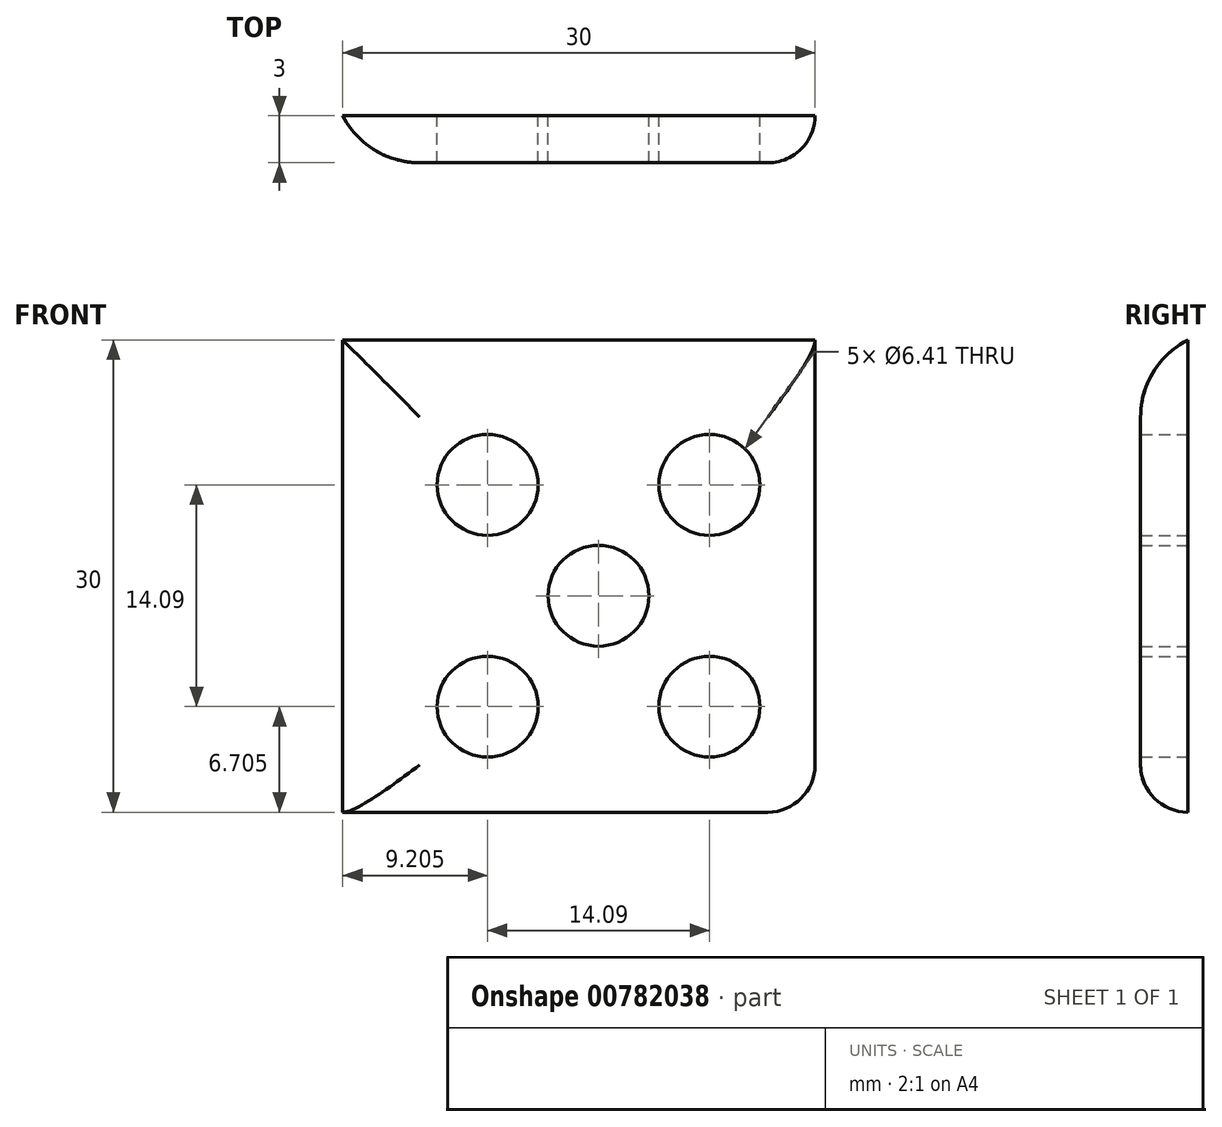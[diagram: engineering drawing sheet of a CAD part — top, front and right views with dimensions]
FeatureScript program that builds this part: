
annotation { "Feature Type Name" : "Feature", "Feature Type Description" : "" }
export const myFeature = defineFeature(function(context is Context, id is Id, definition is map)
    precondition{}
    {
        {
            var Q0;
            Q0=qCreatedBy(makeId("Front.planeOp"),FACE);
            var sketch = newSketch(context, id + "F0", { "sketchPlane" : qUnion([Q0])});
            skLineSegment(sketch, "E0.bottom", {"start": v(0, 0) * mm, "end": v(27, 0) * mm});
            skLineSegment(sketch, "E0.top", {"start": v(0, 30) * mm, "end": v(30, 30) * mm});
            skLineSegment(sketch, "E0.left", {"start": v(0, 0) * mm, "end": v(0, 30) * mm});
            skLineSegment(sketch, "E0.right", {"start": v(30, 3) * mm, "end": v(30, 30) * mm});
            skPoint(sketch, "E1", {"position": v(5.5, 30) * mm});
            skPoint(sketch, "E2", {"position": v(0, 24.5) * mm});
            skPoint(sketch, "E3", {"position": v(0, 3) * mm});
            skPoint(sketch, "E4", {"position": v(5.5, 0) * mm});
            skPoint(sketch, "E5", {"position": v(27, 0) * mm});
            skPoint(sketch, "E6", {"position": v(30, 3) * mm});
            skPoint(sketch, "E7", {"position": v(30, 24.5) * mm});
            skPoint(sketch, "E8", {"position": v(27, 30) * mm});
            skLineSegment(sketch, "E9", {"start": v(5.5, 0) * mm, "end": v(5.5, 30) * mm});
            skLineSegment(sketch, "E10", {"start": v(0, 24.5) * mm, "end": v(30, 24.5) * mm});
            skLineSegment(sketch, "E11", {"start": v(27, 30) * mm, "end": v(27, 0) * mm});
            skLineSegment(sketch, "E12", {"start": v(30, 3) * mm, "end": v(0, 3) * mm});
            skCircle(sketch, "E13", {"center": v(9.2, 6.7) * mm, "radius": 3.2 * mm});
            skCircle(sketch, "E14", {"center": v(23.3, 6.7) * mm, "radius": 3.2 * mm});
            skCircle(sketch, "E15", {"center": v(9.2, 20.8) * mm, "radius": 3.2 * mm});
            skCircle(sketch, "E16", {"center": v(23.3, 20.8) * mm, "radius": 3.2 * mm});
            skPoint(sketch, "E17", {"position": v(5.5, 24.5) * mm});
            skPoint(sketch, "E18", {"position": v(27, 24.5) * mm});
            skPoint(sketch, "E19", {"position": v(27, 3) * mm});
            skPoint(sketch, "E20", {"position": v(5.5, 3) * mm});
            skLineSegment(sketch, "E21", {"start": v(9.2, 6.7) * mm, "end": v(23.3, 20.8) * mm});
            skLineSegment(sketch, "E22", {"start": v(9.2, 20.8) * mm, "end": v(23.3, 6.7) * mm});
            skPoint(sketch, "E23", {"position": v(16.25, 13.75) * mm});
            skCircle(sketch, "E24", {"center": v(16.25, 13.75) * mm, "radius": 3.2 * mm});
            skPoint(sketch, "E25", {"position": v(13.98, 16.02) * mm});
            skPoint(sketch, "E26", {"position": v(11.47, 18.53) * mm});
            skPoint(sketch, "E27.visualSharp", {"position": v(30, 0) * mm});
            skArc(sketch, "E27.filletArc", {"start": v(27, 0) * mm, "mid": v(29.12, 0.88) * mm, "end": v(30, 3) * mm});
            skSolve(sketch);
        }
        {
            var Q0;
            Q0=makeQuery(id+"F0.imprint","IMPRINT",FACE,{"disambiguationData":[TD([[makeQuery(id+"F0.imprint","IMPRINT",EDGE,{"derivedFrom":sQuery(id+"F0.wireOp",EDGE,"E13")}),-1.0]])]});
            var Q1;
            {var subQ0=sQuery(id+"F0.wireOp",EDGE,"E10");var subQ1=sQuery(id+"F0.wireOp",EDGE,"E0.left");var subQ2=makeQuery(id+"F0.imprint","INTERSECT",VERTEX,{"derivedFrom":[subQ1,subQ0]});Q1=makeQuery(id+"F0.imprint","IMPRINT",FACE,{"disambiguationData":[TD([[makeQuery(id+"F0.imprint","IMPRINT",EDGE,{"disambiguationData":[TD([[subQ2,1.0]])],"derivedFrom":subQ1}),-1.0]])]});}
            var Q2;
            {var subQ0=sQuery(id+"F0.wireOp",EDGE,"E0.left");var subQ1=sQuery(id+"F0.wireOp",EDGE,"E0.top");var subQ2=makeQuery(id+"F0.imprint","INTERSECT",VERTEX,{"derivedFrom":[subQ1,subQ0]});Q2=makeQuery(id+"F0.imprint","IMPRINT",FACE,{"disambiguationData":[TD([[makeQuery(id+"F0.imprint","IMPRINT",EDGE,{"disambiguationData":[TD([[subQ2,-1.0]])],"derivedFrom":subQ1}),-1.0]])]});}
            var Q3;
            {var subQ0=sQuery(id+"F0.wireOp",EDGE,"E9");var subQ1=sQuery(id+"F0.wireOp",EDGE,"E0.top");var subQ2=makeQuery(id+"F0.imprint","INTERSECT",VERTEX,{"derivedFrom":[subQ1,subQ0]});Q3=makeQuery(id+"F0.imprint","IMPRINT",FACE,{"disambiguationData":[TD([[makeQuery(id+"F0.imprint","IMPRINT",EDGE,{"disambiguationData":[TD([[subQ2,-1.0]])],"derivedFrom":subQ1}),-1.0]])]});}
            var Q4;
            {var subQ0=sQuery(id+"F0.wireOp",EDGE,"E0.right");var subQ1=sQuery(id+"F0.wireOp",EDGE,"E0.top");var subQ2=makeQuery(id+"F0.imprint","INTERSECT",VERTEX,{"derivedFrom":[subQ1,subQ0]});Q4=makeQuery(id+"F0.imprint","IMPRINT",FACE,{"disambiguationData":[TD([[makeQuery(id+"F0.imprint","IMPRINT",EDGE,{"disambiguationData":[TD([[subQ2,1.0]])],"derivedFrom":subQ1}),-1.0]])]});}
            var Q5;
            {var subQ1=sQuery(id+"F0.wireOp",EDGE,"E0.right");var subQ3=sQuery(id+"F0.wireOp",EDGE,"E10");var subQ4=makeQuery(id+"F0.imprint","INTERSECT",VERTEX,{"derivedFrom":[subQ1,subQ3]});Q5=makeQuery(id+"F0.imprint","IMPRINT",FACE,{"disambiguationData":[TD([[makeQuery(id+"F0.imprint","IMPRINT",EDGE,{"disambiguationData":[TD([[subQ4,1.0]])],"derivedFrom":subQ3}),-1.0]])]});}
            var Q6;
            {var subQ0=sQuery(id+"F0.wireOp",EDGE,"E27.filletArc");Q6=makeQuery(id+"F0.imprint","IMPRINT",FACE,{"disambiguationData":[TD([[makeQuery(id+"F0.imprint","IMPRINT",EDGE,{"derivedFrom":subQ0}),1.0]])]});}
            var Q7;
            {var subQ1=sQuery(id+"F0.wireOp",EDGE,"E0.bottom");var subQ3=sQuery(id+"F0.wireOp",EDGE,"E9");var subQ4=makeQuery(id+"F0.imprint","INTERSECT",VERTEX,{"derivedFrom":[subQ1,subQ3]});Q7=makeQuery(id+"F0.imprint","IMPRINT",FACE,{"disambiguationData":[TD([[makeQuery(id+"F0.imprint","IMPRINT",EDGE,{"disambiguationData":[TD([[subQ4,-1.0]])],"derivedFrom":subQ3}),-1.0]])]});}
            var Q8;
            {var subQ0=sQuery(id+"F0.wireOp",EDGE,"E0.left");var subQ1=sQuery(id+"F0.wireOp",EDGE,"E0.bottom");var subQ2=makeQuery(id+"F0.imprint","INTERSECT",VERTEX,{"derivedFrom":[subQ1,subQ0]});Q8=makeQuery(id+"F0.imprint","IMPRINT",FACE,{"disambiguationData":[TD([[makeQuery(id+"F0.imprint","IMPRINT",EDGE,{"disambiguationData":[TD([[subQ2,-1.0]])],"derivedFrom":subQ1}),1.0]])]});}
            extrude(context, id + "F1", {"entities" : qUnion([Q0, Q1, Q2, Q3, Q4, Q5, Q6, Q7, Q8]), "depth" : 3 * mm, "offsetDistance" : 25 * mm});
        }
        {
            var Q0;
            Q0=makeQuery(id+"F1.opExtrude","CAP_EDGE",EDGE,{"disambiguationData":[OSD([sQuery(id+"F0.wireOp",EDGE,"E27.filletArc")])],"isStart":false});
            var Q1;
            Q1=makeQuery(id+"F1.opExtrude","CAP_EDGE",EDGE,{"disambiguationData":[OSD([sQuery(id+"F0.wireOp",EDGE,"E0.bottom")])],"isStart":false});
            var Q2;
            Q2=makeQuery(id+"F1.opExtrude","CAP_EDGE",EDGE,{"disambiguationData":[OSD([sQuery(id+"F0.wireOp",EDGE,"E0.right")])],"isStart":false});
            fillet(context, id + "F2", {"entities" : qUnion([Q0, Q1, Q2]), "radius" : 3 * mm, "tangentPropagation" : true, "allowEdgeOverflow" : false});
        }
        {
            var Q0;
            Q0=makeQuery(id+"F1.opExtrude","CAP_EDGE",EDGE,{"disambiguationData":[OSD([sQuery(id+"F0.wireOp",EDGE,"E0.left")])],"isStart":false});
            fillet(context, id + "F3", {"entities" : qUnion([Q0]), "radius" : 5.5 * mm, "allowEdgeOverflow" : false});
        }
        {
            var Q0;
            Q0=makeQuery(id+"F1.opExtrude","CAP_EDGE",EDGE,{"disambiguationData":[OSD([sQuery(id+"F0.wireOp",EDGE,"E0.top")])],"isStart":false});
            fillet(context, id + "F4", {"entities" : qUnion([Q0]), "radius" : 5.5 * mm, "allowEdgeOverflow" : false});
        }
    });
